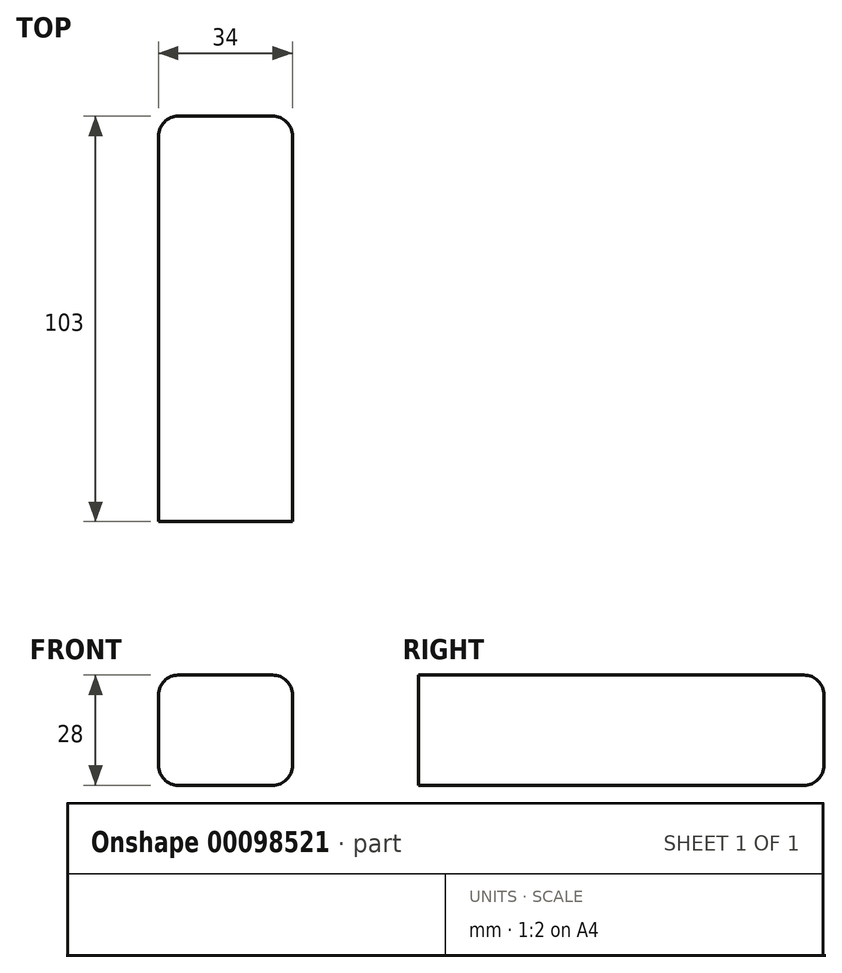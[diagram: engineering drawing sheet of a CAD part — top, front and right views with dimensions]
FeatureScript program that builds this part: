
annotation { "Feature Type Name" : "Feature", "Feature Type Description" : "" }
export const myFeature = defineFeature(function(context is Context, id is Id, definition is map)
    precondition{}
    {
        {
            var Q0;
            Q0=qCreatedBy(makeId("Top.planeOp"),FACE);
            var sketch = newSketch(context, id + "F0", { "sketchPlane" : qUnion([Q0])});
            skLineSegment(sketch, "E0.bottom", {"start": v(0, 0) * mm, "end": v(34, 0) * mm});
            skLineSegment(sketch, "E0.top", {"start": v(0, -103) * mm, "end": v(34, -103) * mm});
            skLineSegment(sketch, "E0.left", {"start": v(0, 0) * mm, "end": v(0, -103) * mm});
            skLineSegment(sketch, "E0.right", {"start": v(34, 0) * mm, "end": v(34, -103) * mm});
            skSolve(sketch);
        }
        {
            var Q0;
            Q0=makeQuery(id+"F0.imprint","IMPRINT",FACE,{"disambiguationData":[TD([[makeQuery(id+"F0.imprint","IMPRINT",EDGE,{"derivedFrom":sQuery(id+"F0.wireOp",EDGE,"E0.bottom")}),-1.0]])]});
            extrude(context, id + "F1", {"entities" : qUnion([Q0]), "depth" : 28 * mm});
        }
        {
            var Q0;
            Q0=makeQuery(id+"F1.opExtrude","CAP_EDGE",EDGE,{"disambiguationData":[OSD([sQuery(id+"F0.wireOp",EDGE,"E0.right")])],"isStart":false});
            var Q1;
            Q1=makeQuery(id+"F1.opExtrude","CAP_EDGE",EDGE,{"disambiguationData":[OSD([sQuery(id+"F0.wireOp",EDGE,"E0.right")])],"isStart":true});
            var Q2;
            Q2=makeQuery(id+"F1.opExtrude","CAP_EDGE",EDGE,{"disambiguationData":[OSD([sQuery(id+"F0.wireOp",EDGE,"E0.left")])],"isStart":false});
            var Q3;
            Q3=makeQuery(id+"F1.opExtrude","CAP_EDGE",EDGE,{"disambiguationData":[OSD([sQuery(id+"F0.wireOp",EDGE,"E0.left")])],"isStart":true});
            var Q4;
            Q4=makeQuery(id+"F1.opExtrude","CAP_EDGE",EDGE,{"disambiguationData":[OSD([sQuery(id+"F0.wireOp",EDGE,"E0.bottom")])],"isStart":true});
            var Q5;
            Q5=makeQuery(id+"F1.opExtrude","SWEPT_FACE",FACE,{"disambiguationData":[OSD([sQuery(id+"F0.wireOp",EDGE,"E0.bottom")])]});
            fillet(context, id + "F2", {"entities" : qUnion([Q0, Q1, Q2, Q3, Q4, Q5]), "radius" : 5 * mm, "tangentPropagation" : true, "allowEdgeOverflow" : false});
        }
    });
